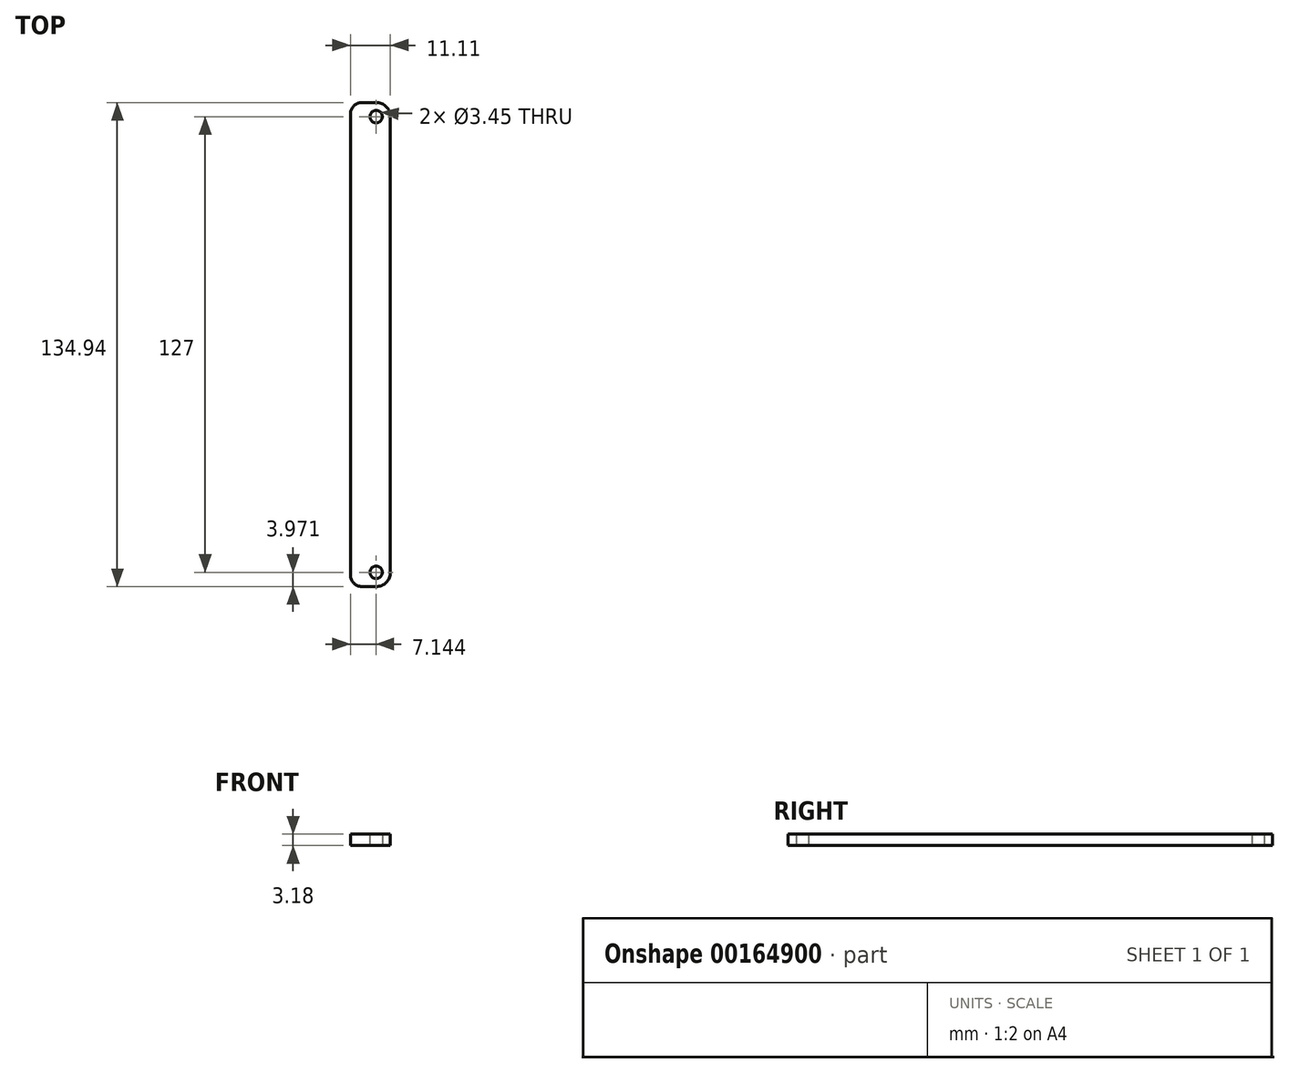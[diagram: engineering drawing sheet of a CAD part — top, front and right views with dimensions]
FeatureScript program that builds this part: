
annotation { "Feature Type Name" : "Feature", "Feature Type Description" : "" }
export const myFeature = defineFeature(function(context is Context, id is Id, definition is map)
    precondition{}
    {
        {
            var Q0;
            Q0=qCreatedBy(makeId("Top.planeOp"),FACE);
            var sketch = newSketch(context, id + "F0", { "sketchPlane" : qUnion([Q0])});
            skLineSegment(sketch, "E0.bottom", {"start": v(0, 0) * mm, "end": v(11.11, 0) * mm});
            skLineSegment(sketch, "E0.top", {"start": v(0, -134.94) * mm, "end": v(11.11, -134.94) * mm});
            skLineSegment(sketch, "E0.left", {"start": v(0, 0) * mm, "end": v(0, -134.94) * mm});
            skLineSegment(sketch, "E0.right", {"start": v(11.11, 0) * mm, "end": v(11.11, -134.94) * mm});
            skLineSegment(sketch, "E1", {"start": v(7.14, 0) * mm, "end": v(7.14, -3.97) * mm, "construction": true});
            skLineSegment(sketch, "E2", {"start": v(7.14, -3.97) * mm, "end": v(11.11, -3.97) * mm, "construction": true});
            skLineSegment(sketch, "E3", {"start": v(7.14, -134.94) * mm, "end": v(7.14, -130.97) * mm, "construction": true});
            skCircle(sketch, "E4", {"center": v(7.14, -3.97) * mm, "radius": 1.73 * mm});
            skCircle(sketch, "E5", {"center": v(7.14, -130.97) * mm, "radius": 1.73 * mm});
            skSolve(sketch);
        }
        {
            var Q0;
            Q0=qSketchRegion(id+"F0",true);
            extrude(context, id + "F1", {"entities" : qUnion([Q0]), "depth" : 3.17 * mm});
        }
        {
            var Q0;
            Q0=makeQuery(id+"F1.opExtrude","SWEPT_EDGE",EDGE,{"disambiguationData":[OSD([sQuery(id+"F0.wireOp",EDGE,"E0.bottom"),sQuery(id+"F0.wireOp",EDGE,"E0.right")])]});
            var Q1;
            Q1=makeQuery(id+"F1.opExtrude","SWEPT_EDGE",EDGE,{"disambiguationData":[OSD([sQuery(id+"F0.wireOp",EDGE,"E0.top"),sQuery(id+"F0.wireOp",EDGE,"E0.right")])]});
            fillet(context, id + "F2", {"entities" : qUnion([Q0, Q1]), "radius" : 3.97 * mm, "tangentPropagation" : true, "allowEdgeOverflow" : false});
        }
        {
            var Q0;
            Q0=makeQuery(id+"F1.opExtrude","SWEPT_EDGE",EDGE,{"disambiguationData":[OSD([sQuery(id+"F0.wireOp",EDGE,"E0.top"),sQuery(id+"F0.wireOp",EDGE,"E0.left")])]});
            var Q1;
            Q1=makeQuery(id+"F1.opExtrude","SWEPT_EDGE",EDGE,{"disambiguationData":[OSD([sQuery(id+"F0.wireOp",EDGE,"E0.bottom"),sQuery(id+"F0.wireOp",EDGE,"E0.left")])]});
            fillet(context, id + "F3", {"entities" : qUnion([Q0, Q1]), "radius" : 3.17 * mm, "tangentPropagation" : true, "allowEdgeOverflow" : false});
        }
    });
